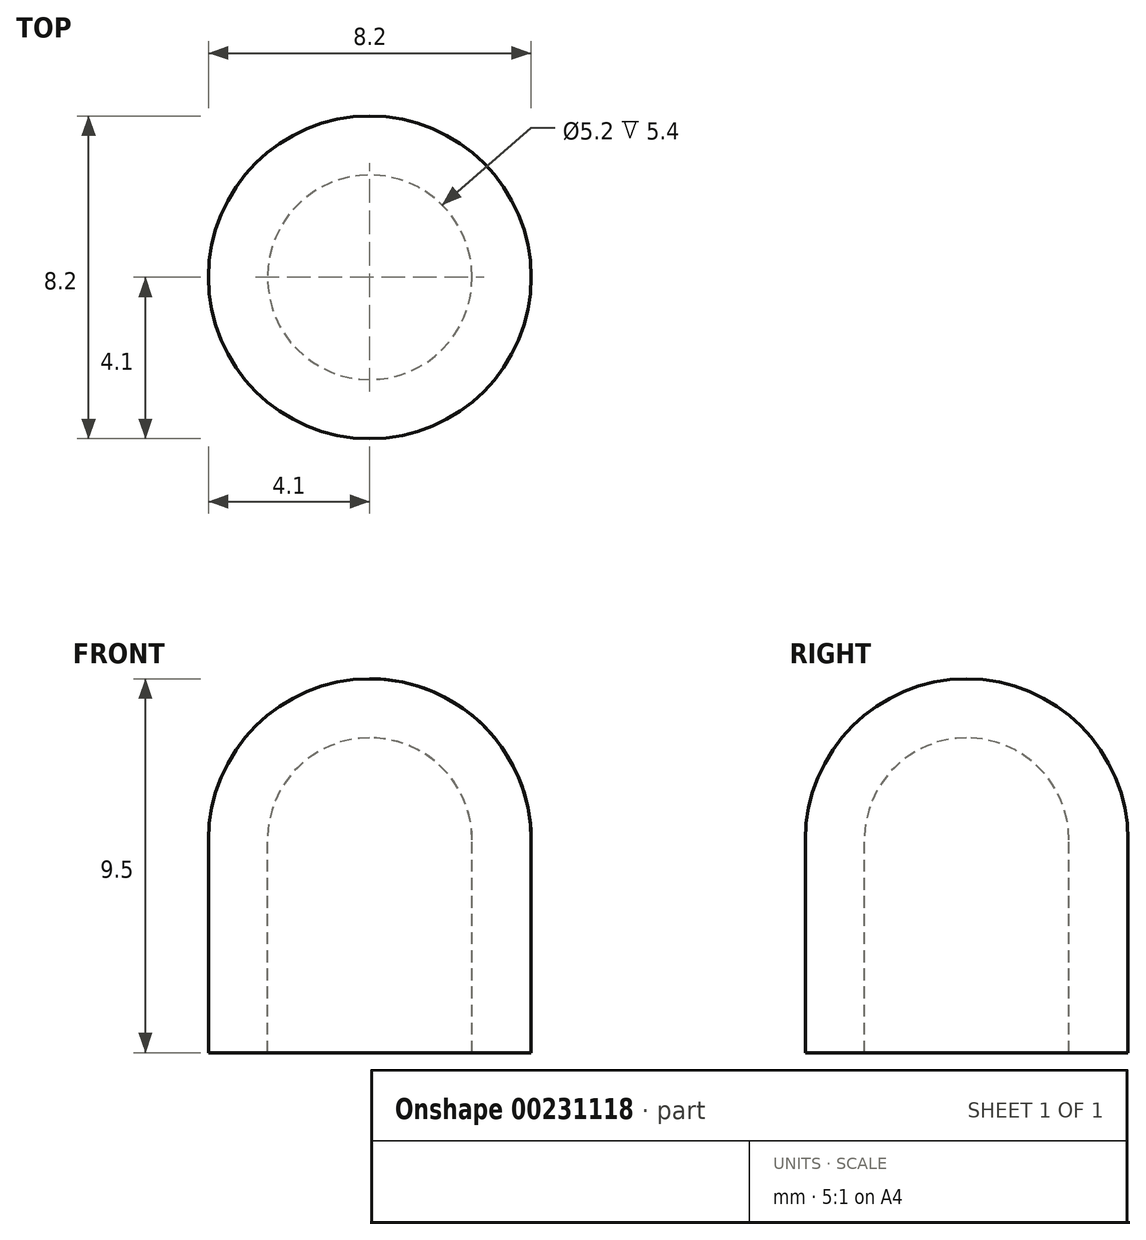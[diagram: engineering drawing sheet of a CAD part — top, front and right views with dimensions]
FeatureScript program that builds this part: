
annotation { "Feature Type Name" : "Feature", "Feature Type Description" : "" }
export const myFeature = defineFeature(function(context is Context, id is Id, definition is map)
    precondition{}
    {
        {
            var Q0;
            Q0=qCreatedBy(makeId("Front.planeOp"),FACE);
            var sketch = newSketch(context, id + "F0", { "sketchPlane" : qUnion([Q0])});
            skLineSegment(sketch, "E0", {"start": v(2.6, 0) * mm, "end": v(2.6, 5.4) * mm});
            skArc(sketch, "E1", {"start": v(2.6, 5.4) * mm, "mid": v(1.84, 7.24) * mm, "end": v(0, 8) * mm});
            skArc(sketch, "E2.0", {"start": v(4.1, 5.4) * mm, "mid": v(2.9, 8.3) * mm, "end": v(0, 9.5) * mm});
            skLineSegment(sketch, "E2.1", {"start": v(4.1, 0) * mm, "end": v(4.1, 5.4) * mm});
            skLineSegment(sketch, "E3", {"start": v(0, 9.5) * mm, "end": v(0, 8) * mm});
            skLineSegment(sketch, "E4", {"start": v(4.1, 0) * mm, "end": v(2.6, 0) * mm});
            skSolve(sketch);
        }
        {
            var Q0;
            Q0 = qSketchRegion(id + "F0", true);
            var Q1;
            Q1=sQuery(id+"F0.wireOp",EDGE,"E3");
            revolve(context, id + "F1", {"entities" : qUnion([Q0]), "axis" : qUnion([Q1]), "revolveType" : RevolveType.FULL});
        }
    });
